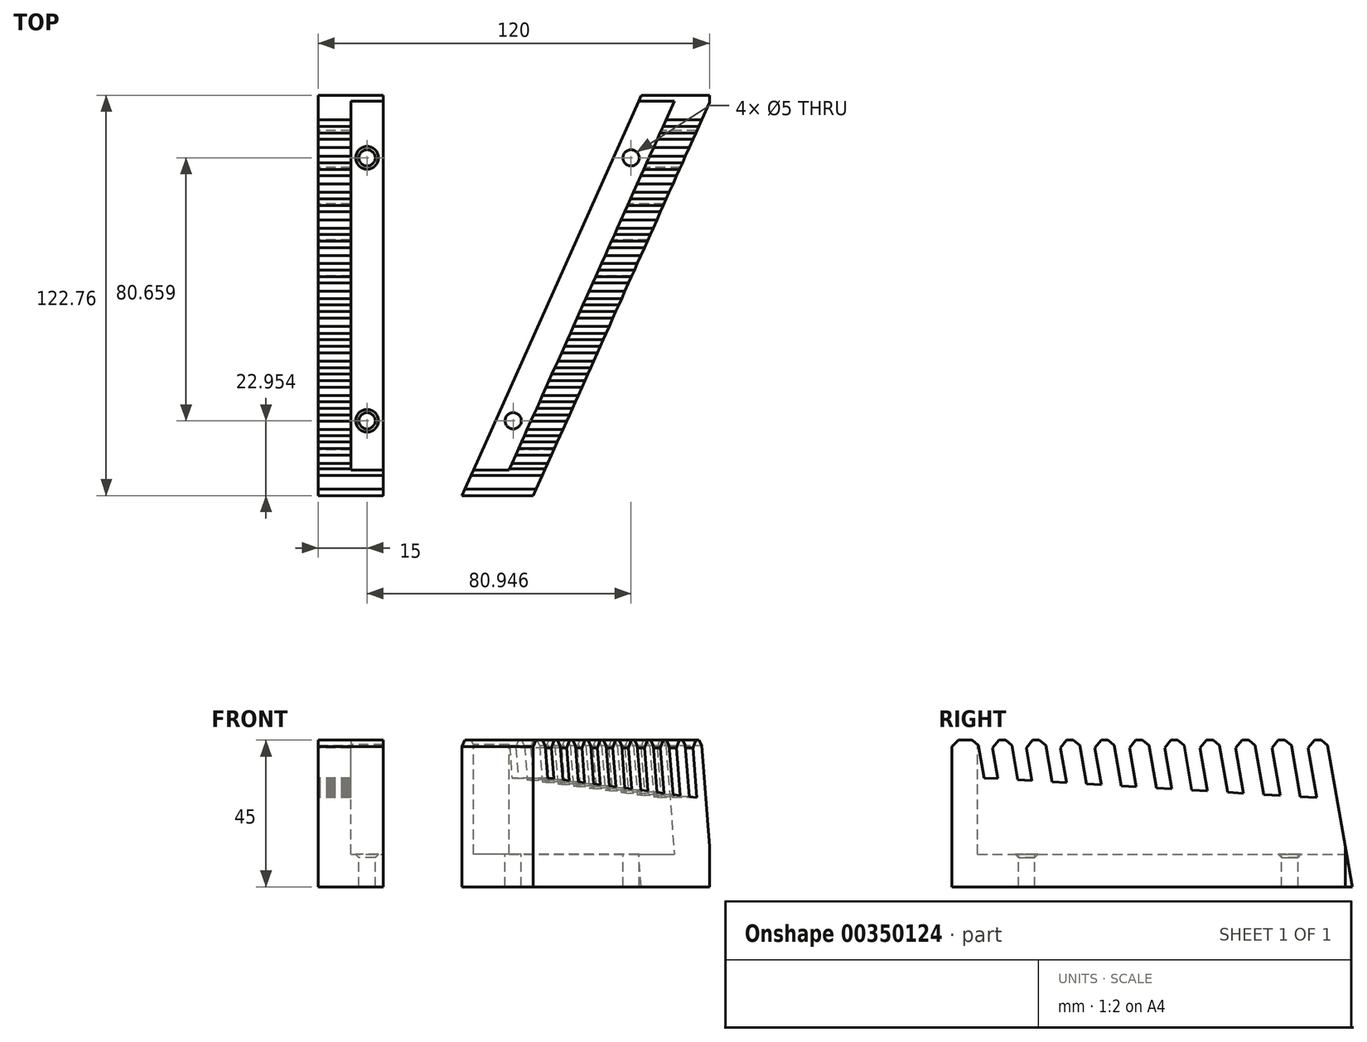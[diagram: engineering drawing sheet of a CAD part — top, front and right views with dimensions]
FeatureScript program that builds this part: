
annotation { "Feature Type Name" : "Feature", "Feature Type Description" : "" }
export const myFeature = defineFeature(function(context is Context, id is Id, definition is map)
    precondition{}
    {
        {
            var Q0;
            Q0=qCreatedBy(makeId("Right.planeOp"),FACE);
            var sketch = newSketch(context, id + "F0", { "sketchPlane" : qUnion([Q0])});
            skLineSegment(sketch, "E0.bottom", {"start": v(0, 0) * mm, "end": v(122.76, 0) * mm});
            skLineSegment(sketch, "E0.top", {"start": v(0, 45) * mm, "end": v(7.9, 45) * mm});
            skLineSegment(sketch, "E0.left", {"start": v(0, 0) * mm, "end": v(0, 45) * mm});
            skLineSegment(sketch, "E1", {"start": v(7.9, 45) * mm, "end": v(9.9, 33.41) * mm});
            skLineSegment(sketch, "E2", {"start": v(12.05, 45) * mm, "end": v(14.1, 33.16) * mm});
            skLineSegment(sketch, "E3", {"start": v(18.14, 45) * mm, "end": v(20.26, 32.8) * mm});
            skLineSegment(sketch, "E4", {"start": v(22.4, 45) * mm, "end": v(24.56, 32.54) * mm});
            skLineSegment(sketch, "E5", {"start": v(28.5, 45) * mm, "end": v(30.72, 32.18) * mm});
            skLineSegment(sketch, "E6", {"start": v(32.86, 45) * mm, "end": v(35.13, 31.92) * mm});
            skLineSegment(sketch, "E7", {"start": v(38.95, 45) * mm, "end": v(41.28, 31.55) * mm});
            skLineSegment(sketch, "E8", {"start": v(43.41, 45) * mm, "end": v(45.8, 31.29) * mm});
            skLineSegment(sketch, "E9", {"start": v(49.5, 45) * mm, "end": v(51.94, 30.92) * mm});
            skLineSegment(sketch, "E10", {"start": v(54.07, 45) * mm, "end": v(56.56, 30.65) * mm});
            skLineSegment(sketch, "E11", {"start": v(60.16, 45) * mm, "end": v(62.71, 30.28) * mm});
            skLineSegment(sketch, "E12", {"start": v(64.83, 45) * mm, "end": v(67.43, 30) * mm});
            skLineSegment(sketch, "E13", {"start": v(70.92, 45) * mm, "end": v(73.58, 29.64) * mm});
            skLineSegment(sketch, "E14", {"start": v(75.69, 45) * mm, "end": v(78.4, 29.35) * mm});
            skLineSegment(sketch, "E15", {"start": v(81.78, 45) * mm, "end": v(84.55, 28.99) * mm});
            skLineSegment(sketch, "E16", {"start": v(86.65, 45) * mm, "end": v(89.47, 28.7) * mm});
            skLineSegment(sketch, "E17", {"start": v(92.74, 45) * mm, "end": v(95.63, 28.33) * mm});
            skLineSegment(sketch, "E18", {"start": v(97.71, 45) * mm, "end": v(100.65, 28.03) * mm});
            skLineSegment(sketch, "E19", {"start": v(103.8, 45) * mm, "end": v(106.8, 27.67) * mm});
            skLineSegment(sketch, "E20", {"start": v(108.88, 45) * mm, "end": v(111.93, 27.36) * mm});
            skLineSegment(sketch, "E21", {"start": v(114.97, 45) * mm, "end": v(117.16, 32.36) * mm});
            skLineSegment(sketch, "E22.trimOffspring", {"start": v(12.05, 45) * mm, "end": v(18.14, 45) * mm});
            skLineSegment(sketch, "E23.trimOffspring", {"start": v(22.4, 45) * mm, "end": v(28.5, 45) * mm});
            skLineSegment(sketch, "E24.trimOffspring", {"start": v(32.86, 45) * mm, "end": v(38.95, 45) * mm});
            skLineSegment(sketch, "E25.trimOffspring", {"start": v(43.41, 45) * mm, "end": v(49.5, 45) * mm});
            skLineSegment(sketch, "E26.trimOffspring", {"start": v(54.07, 45) * mm, "end": v(60.16, 45) * mm});
            skLineSegment(sketch, "E27.trimOffspring", {"start": v(64.83, 45) * mm, "end": v(70.92, 45) * mm});
            skLineSegment(sketch, "E28.trimOffspring", {"start": v(75.69, 45) * mm, "end": v(81.78, 45) * mm});
            skLineSegment(sketch, "E29.trimOffspring", {"start": v(86.65, 45) * mm, "end": v(92.74, 45) * mm});
            skLineSegment(sketch, "E30.trimOffspring", {"start": v(97.71, 45) * mm, "end": v(103.8, 45) * mm});
            skLineSegment(sketch, "E31.trimOffspring", {"start": v(108.88, 45) * mm, "end": v(114.97, 45) * mm});
            skLineSegment(sketch, "E32.trimOffspring", {"start": v(163.56, 45) * mm, "end": v(163.58, 45) * mm});
            skLineSegment(sketch, "E33", {"start": v(114.97, 45) * mm, "end": v(122.76, 0) * mm});
            skLineSegment(sketch, "E34", {"start": v(9.9, 33.41) * mm, "end": v(14.1, 33.16) * mm});
            skPoint(sketch, "E35.orphan", {"position": v(0, 34) * mm});
            skLineSegment(sketch, "E36.trimOffspring", {"start": v(20.26, 32.8) * mm, "end": v(24.56, 32.54) * mm});
            skLineSegment(sketch, "E37.trimOffspring", {"start": v(30.72, 32.18) * mm, "end": v(35.13, 31.92) * mm});
            skLineSegment(sketch, "E38.trimOffspring", {"start": v(41.28, 31.55) * mm, "end": v(45.8, 31.29) * mm});
            skLineSegment(sketch, "E39.trimOffspring", {"start": v(51.94, 30.92) * mm, "end": v(56.56, 30.65) * mm});
            skLineSegment(sketch, "E40.trimOffspring", {"start": v(62.71, 30.28) * mm, "end": v(67.43, 30) * mm});
            skLineSegment(sketch, "E41.trimOffspring", {"start": v(73.58, 29.64) * mm, "end": v(78.4, 29.35) * mm});
            skLineSegment(sketch, "E42.trimOffspring", {"start": v(84.55, 28.99) * mm, "end": v(89.47, 28.7) * mm});
            skLineSegment(sketch, "E43.trimOffspring", {"start": v(106.8, 27.67) * mm, "end": v(111.93, 27.36) * mm});
            skPoint(sketch, "E44.orphan", {"position": v(118.08, 27) * mm});
            skLineSegment(sketch, "E45", {"start": v(95.63, 28.33) * mm, "end": v(100.65, 28.03) * mm});
            skSolve(sketch);
        }
        {
            var Q0;
            Q0 = qSketchRegion(id + "F0", true);
            extrude(context, id + "F1", {"entities" : qUnion([Q0]), "depth" : 120 * mm});
        }
        {
            var Q0;
            Q0=makeQuery(id+"F1.opExtrude","SWEPT_FACE",FACE,{"disambiguationData":[OSD([sQuery(id+"F0.wireOp",EDGE,"E0.top")])]});
            var sketch = newSketch(context, id + "F2", { "sketchPlane" : qUnion([Q0])});
            skLineSegment(sketch, "E46", {"start": v(10, 122.56) * mm, "end": v(10, 0) * mm});
            skLineSegment(sketch, "E47", {"start": v(55, 0) * mm, "end": v(110, 122.75) * mm});
            skLineSegment(sketch, "E48", {"start": v(120.96, 122.75) * mm, "end": v(65.96, 0) * mm});
            skLineSegment(sketch, "E49", {"start": v(65.96, 0) * mm, "end": v(120, 0) * mm});
            skLineSegment(sketch, "E50", {"start": v(120.96, 122.75) * mm, "end": v(120.96, 0) * mm});
            skLineSegment(sketch, "E51", {"start": v(120.96, 0) * mm, "end": v(65.96, 0) * mm});
            skLineSegment(sketch, "E52", {"start": v(55, 0) * mm, "end": v(10, 0) * mm});
            skLineSegment(sketch, "E53", {"start": v(110, 122.75) * mm, "end": v(10, 122.56) * mm});
            skLineSegment(sketch, "E54", {"start": v(10, 0) * mm, "end": v(55, 0) * mm});
            skSolve(sketch);
        }
        {
            var Q0;
            {var subQ2=sQuery(id+"F0.wireOp",EDGE,"E0.top");var subQ6=makeQuery(id+"F1.opExtrude","CAP_EDGE",EDGE,{"disambiguationData":[OSD([subQ2])],"isStart":false});Q0=makeQuery(id+"F2.imprint","IMPRINT",FACE,{"disambiguationData":[TD([[makeQuery(id+"F2.imprint","IMPRINT",EDGE,{"derivedFrom":subQ6}),1.0]])]});}
            var Q1;
            {var subQ3=sQuery(id+"F2.wireOp",EDGE,"E50");Q1=makeQuery(id+"F2.imprint","IMPRINT",FACE,{"disambiguationData":[TD([[makeQuery(id+"F2.imprint","IMPRINT",EDGE,{"derivedFrom":subQ3}),-1.0]])]});}
            extrude(context, id + "F3", {"entities" : qUnion([Q0, Q1]), "operationType" : NewBodyOperationType.REMOVE, "endBound" : BoundingType.THROUGH_ALL, "oppositeDirection" : true, "depth" : 25 * mm});
        }
        {
            var Q0;
            {var subQ0=sQuery(id+"F2.wireOp",EDGE,"E53");Q0=makeQuery(id+"F2.imprint","IMPRINT",FACE,{"disambiguationData":[TD([[makeQuery(id+"F2.imprint","IMPRINT",EDGE,{"derivedFrom":subQ0}),1.0]])]});}
            var Q1;
            {var subQ0=sQuery(id+"F2.wireOp",EDGE,"E54");Q1=makeQuery(id+"F2.imprint","IMPRINT",FACE,{"disambiguationData":[TD([[makeQuery(id+"F2.imprint","IMPRINT",EDGE,{"derivedFrom":subQ0}),-1.0]])]});}
            extrude(context, id + "F4", {"entities" : qUnion([Q0, Q1]), "operationType" : NewBodyOperationType.REMOVE, "oppositeDirection" : true, "depth" : 35 * mm});
        }
        {
            var Q0;
            {var subQ0=sQuery(id+"F2.wireOp",EDGE,"E53");Q0=makeQuery(id+"F2.imprint","IMPRINT",FACE,{"disambiguationData":[TD([[makeQuery(id+"F2.imprint","IMPRINT",EDGE,{"derivedFrom":subQ0}),1.0]])]});}
            var sketch = newSketch(context, id + "F5", { "sketchPlane" : qUnion([Q0])});
            skLineSegment(sketch, "E55", {"start": v(20, 127.84) * mm, "end": v(20, -6.7) * mm});
            skLineSegment(sketch, "E56", {"start": v(101.32, 127.84) * mm, "end": v(41.04, -6.7) * mm});
            skLineSegment(sketch, "E57", {"start": v(20, 127.84) * mm, "end": v(101.32, 127.84) * mm});
            skLineSegment(sketch, "E58", {"start": v(20, -6.7) * mm, "end": v(41.04, -6.7) * mm});
            skSolve(sketch);
        }
        {
            var Q0;
            Q0 = qSketchRegion(id + "F5", true);
            extrude(context, id + "F6", {"entities" : qUnion([Q0]), "operationType" : NewBodyOperationType.REMOVE, "endBound" : BoundingType.THROUGH_ALL, "oppositeDirection" : true, "depth" : 25 * mm});
        }
        {
            var Q0;
            {var subQ0=sQuery(id+"F2.wireOp",EDGE,"E53");Q0=makeQuery(id+"F2.imprint","IMPRINT",FACE,{"disambiguationData":[TD([[makeQuery(id+"F2.imprint","IMPRINT",EDGE,{"derivedFrom":subQ0}),1.0]])]});}
            var sketch = newSketch(context, id + "F7", { "sketchPlane" : qUnion([Q0])});
            skCircle(sketch, "E59", {"center": v(15, 103.61) * mm, "radius": 2.5 * mm});
            skCircle(sketch, "E60", {"center": v(15, 22.95) * mm, "radius": 2.5 * mm});
            skCircle(sketch, "E61", {"center": v(95.95, 103.61) * mm, "radius": 2.5 * mm});
            skCircle(sketch, "E62", {"center": v(59.8, 22.95) * mm, "radius": 2.5 * mm});
            skSolve(sketch);
        }
        {
            var Q0;
            Q0=makeQuery(id+"F7.imprint","IMPRINT",FACE,{"disambiguationData":[TD([[makeQuery(id+"F7.imprint","IMPRINT",EDGE,{"derivedFrom":sQuery(id+"F7.wireOp",EDGE,"E59")}),1.0]])]});
            var Q1;
            Q1=makeQuery(id+"F7.imprint","IMPRINT",FACE,{"disambiguationData":[TD([[makeQuery(id+"F7.imprint","IMPRINT",EDGE,{"derivedFrom":sQuery(id+"F7.wireOp",EDGE,"E61")}),1.0]])]});
            var Q2;
            Q2=makeQuery(id+"F7.imprint","IMPRINT",FACE,{"disambiguationData":[TD([[makeQuery(id+"F7.imprint","IMPRINT",EDGE,{"derivedFrom":sQuery(id+"F7.wireOp",EDGE,"E60")}),1.0]])]});
            var Q3;
            Q3=makeQuery(id+"F7.imprint","IMPRINT",FACE,{"disambiguationData":[TD([[makeQuery(id+"F7.imprint","IMPRINT",EDGE,{"derivedFrom":sQuery(id+"F7.wireOp",EDGE,"E62")}),1.0]])]});
            extrude(context, id + "F8", {"entities" : qUnion([Q0, Q1, Q2, Q3]), "operationType" : NewBodyOperationType.REMOVE, "oppositeDirection" : true, "depth" : 55.9 * mm});
        }
        {
            var Q0;
            Q0=makeQuery(id+"F7.imprint","IMPRINT",FACE,{"disambiguationData":[TD([[makeQuery(id+"F7.imprint","IMPRINT",EDGE,{"derivedFrom":sQuery(id+"F7.wireOp",EDGE,"E61")}),1.0]])]});
            var Q1;
            Q1=makeQuery(id+"F7.imprint","IMPRINT",FACE,{"disambiguationData":[TD([[makeQuery(id+"F7.imprint","IMPRINT",EDGE,{"derivedFrom":sQuery(id+"F7.wireOp",EDGE,"E62")}),1.0]])]});
            extrude(context, id + "F9", {"entities" : qUnion([Q0, Q1]), "operationType" : NewBodyOperationType.REMOVE, "oppositeDirection" : true, "depth" : 56 * mm});
        }
        {
            var Q0;
            {var subQ0=sQuery(id+"F0.wireOp",EDGE,"E33");var subQ1=sQuery(id+"F0.wireOp",EDGE,"E31.trimOffspring");Q0=makeQuery(id+"F4.boolean.opBoolean","SPLIT",EDGE,{"disambiguationData":[TD([makeQuery(id+"F4.opExtrude","SWEPT_FACE",FACE,{"disambiguationData":[OSD([sQuery(id+"F2.wireOp",EDGE,"E46")])]})])],"derivedFrom":makeQuery(id+"F1.opExtrude","SWEPT_EDGE",EDGE,{"disambiguationData":[OSD([subQ1,subQ0])]})});}
            var Q1;
            {var subQ0=sQuery(id+"F0.wireOp",EDGE,"E31.trimOffspring");var subQ1=sQuery(id+"F0.wireOp",EDGE,"E20");Q1=makeQuery(id+"F4.boolean.opBoolean","SPLIT",EDGE,{"disambiguationData":[TD([makeQuery(id+"F4.opExtrude","SWEPT_FACE",FACE,{"disambiguationData":[OSD([sQuery(id+"F2.wireOp",EDGE,"E46")])]})])],"derivedFrom":makeQuery(id+"F1.opExtrude","SWEPT_EDGE",EDGE,{"disambiguationData":[OSD([subQ1,subQ0])]})});}
            var Q2;
            {var subQ0=sQuery(id+"F0.wireOp",EDGE,"E30.trimOffspring");var subQ1=sQuery(id+"F0.wireOp",EDGE,"E19");Q2=makeQuery(id+"F4.boolean.opBoolean","SPLIT",EDGE,{"disambiguationData":[TD([makeQuery(id+"F4.opExtrude","SWEPT_FACE",FACE,{"disambiguationData":[OSD([sQuery(id+"F2.wireOp",EDGE,"E46")])]})])],"derivedFrom":makeQuery(id+"F1.opExtrude","SWEPT_EDGE",EDGE,{"disambiguationData":[OSD([subQ1,subQ0])]})});}
            var Q3;
            {var subQ0=sQuery(id+"F0.wireOp",EDGE,"E30.trimOffspring");var subQ1=sQuery(id+"F0.wireOp",EDGE,"E18");Q3=makeQuery(id+"F4.boolean.opBoolean","SPLIT",EDGE,{"disambiguationData":[TD([makeQuery(id+"F4.opExtrude","SWEPT_FACE",FACE,{"disambiguationData":[OSD([sQuery(id+"F2.wireOp",EDGE,"E46")])]})])],"derivedFrom":makeQuery(id+"F1.opExtrude","SWEPT_EDGE",EDGE,{"disambiguationData":[OSD([subQ1,subQ0])]})});}
            var Q4;
            {var subQ0=sQuery(id+"F0.wireOp",EDGE,"E29.trimOffspring");var subQ1=sQuery(id+"F0.wireOp",EDGE,"E17");Q4=makeQuery(id+"F4.boolean.opBoolean","SPLIT",EDGE,{"disambiguationData":[TD([makeQuery(id+"F4.opExtrude","SWEPT_FACE",FACE,{"disambiguationData":[OSD([sQuery(id+"F2.wireOp",EDGE,"E46")])]})])],"derivedFrom":makeQuery(id+"F1.opExtrude","SWEPT_EDGE",EDGE,{"disambiguationData":[OSD([subQ1,subQ0])]})});}
            var Q5;
            {var subQ0=sQuery(id+"F0.wireOp",EDGE,"E29.trimOffspring");var subQ1=sQuery(id+"F0.wireOp",EDGE,"E16");Q5=makeQuery(id+"F4.boolean.opBoolean","SPLIT",EDGE,{"disambiguationData":[TD([makeQuery(id+"F4.opExtrude","SWEPT_FACE",FACE,{"disambiguationData":[OSD([sQuery(id+"F2.wireOp",EDGE,"E46")])]})])],"derivedFrom":makeQuery(id+"F1.opExtrude","SWEPT_EDGE",EDGE,{"disambiguationData":[OSD([subQ1,subQ0])]})});}
            var Q6;
            {var subQ0=sQuery(id+"F0.wireOp",EDGE,"E28.trimOffspring");var subQ1=sQuery(id+"F0.wireOp",EDGE,"E15");Q6=makeQuery(id+"F4.boolean.opBoolean","SPLIT",EDGE,{"disambiguationData":[TD([makeQuery(id+"F4.opExtrude","SWEPT_FACE",FACE,{"disambiguationData":[OSD([sQuery(id+"F2.wireOp",EDGE,"E46")])]})])],"derivedFrom":makeQuery(id+"F1.opExtrude","SWEPT_EDGE",EDGE,{"disambiguationData":[OSD([subQ1,subQ0])]})});}
            var Q7;
            {var subQ0=sQuery(id+"F0.wireOp",EDGE,"E28.trimOffspring");var subQ1=sQuery(id+"F0.wireOp",EDGE,"E14");Q7=makeQuery(id+"F4.boolean.opBoolean","SPLIT",EDGE,{"disambiguationData":[TD([makeQuery(id+"F4.opExtrude","SWEPT_FACE",FACE,{"disambiguationData":[OSD([sQuery(id+"F2.wireOp",EDGE,"E46")])]})])],"derivedFrom":makeQuery(id+"F1.opExtrude","SWEPT_EDGE",EDGE,{"disambiguationData":[OSD([subQ1,subQ0])]})});}
            var Q8;
            {var subQ0=sQuery(id+"F0.wireOp",EDGE,"E27.trimOffspring");var subQ1=sQuery(id+"F0.wireOp",EDGE,"E13");Q8=makeQuery(id+"F4.boolean.opBoolean","SPLIT",EDGE,{"disambiguationData":[TD([makeQuery(id+"F4.opExtrude","SWEPT_FACE",FACE,{"disambiguationData":[OSD([sQuery(id+"F2.wireOp",EDGE,"E46")])]})])],"derivedFrom":makeQuery(id+"F1.opExtrude","SWEPT_EDGE",EDGE,{"disambiguationData":[OSD([subQ1,subQ0])]})});}
            var Q9;
            {var subQ0=sQuery(id+"F0.wireOp",EDGE,"E27.trimOffspring");var subQ1=sQuery(id+"F0.wireOp",EDGE,"E12");Q9=makeQuery(id+"F4.boolean.opBoolean","SPLIT",EDGE,{"disambiguationData":[TD([makeQuery(id+"F4.opExtrude","SWEPT_FACE",FACE,{"disambiguationData":[OSD([sQuery(id+"F2.wireOp",EDGE,"E46")])]})])],"derivedFrom":makeQuery(id+"F1.opExtrude","SWEPT_EDGE",EDGE,{"disambiguationData":[OSD([subQ1,subQ0])]})});}
            var Q10;
            {var subQ0=sQuery(id+"F0.wireOp",EDGE,"E26.trimOffspring");var subQ1=sQuery(id+"F0.wireOp",EDGE,"E11");Q10=makeQuery(id+"F4.boolean.opBoolean","SPLIT",EDGE,{"disambiguationData":[TD([makeQuery(id+"F4.opExtrude","SWEPT_FACE",FACE,{"disambiguationData":[OSD([sQuery(id+"F2.wireOp",EDGE,"E46")])]})])],"derivedFrom":makeQuery(id+"F1.opExtrude","SWEPT_EDGE",EDGE,{"disambiguationData":[OSD([subQ1,subQ0])]})});}
            var Q11;
            {var subQ0=sQuery(id+"F0.wireOp",EDGE,"E26.trimOffspring");var subQ1=sQuery(id+"F0.wireOp",EDGE,"E10");Q11=makeQuery(id+"F4.boolean.opBoolean","SPLIT",EDGE,{"disambiguationData":[TD([makeQuery(id+"F4.opExtrude","SWEPT_FACE",FACE,{"disambiguationData":[OSD([sQuery(id+"F2.wireOp",EDGE,"E46")])]})])],"derivedFrom":makeQuery(id+"F1.opExtrude","SWEPT_EDGE",EDGE,{"disambiguationData":[OSD([subQ1,subQ0])]})});}
            var Q12;
            {var subQ0=sQuery(id+"F0.wireOp",EDGE,"E25.trimOffspring");var subQ1=sQuery(id+"F0.wireOp",EDGE,"E9");Q12=makeQuery(id+"F4.boolean.opBoolean","SPLIT",EDGE,{"disambiguationData":[TD([makeQuery(id+"F4.opExtrude","SWEPT_FACE",FACE,{"disambiguationData":[OSD([sQuery(id+"F2.wireOp",EDGE,"E46")])]})])],"derivedFrom":makeQuery(id+"F1.opExtrude","SWEPT_EDGE",EDGE,{"disambiguationData":[OSD([subQ1,subQ0])]})});}
            var Q13;
            {var subQ0=sQuery(id+"F0.wireOp",EDGE,"E25.trimOffspring");var subQ1=sQuery(id+"F0.wireOp",EDGE,"E8");Q13=makeQuery(id+"F4.boolean.opBoolean","SPLIT",EDGE,{"disambiguationData":[TD([makeQuery(id+"F4.opExtrude","SWEPT_FACE",FACE,{"disambiguationData":[OSD([sQuery(id+"F2.wireOp",EDGE,"E46")])]})])],"derivedFrom":makeQuery(id+"F1.opExtrude","SWEPT_EDGE",EDGE,{"disambiguationData":[OSD([subQ1,subQ0])]})});}
            var Q14;
            {var subQ0=sQuery(id+"F0.wireOp",EDGE,"E24.trimOffspring");var subQ1=sQuery(id+"F0.wireOp",EDGE,"E7");Q14=makeQuery(id+"F4.boolean.opBoolean","SPLIT",EDGE,{"disambiguationData":[TD([makeQuery(id+"F4.opExtrude","SWEPT_FACE",FACE,{"disambiguationData":[OSD([sQuery(id+"F2.wireOp",EDGE,"E46")])]})])],"derivedFrom":makeQuery(id+"F1.opExtrude","SWEPT_EDGE",EDGE,{"disambiguationData":[OSD([subQ1,subQ0])]})});}
            var Q15;
            {var subQ0=sQuery(id+"F0.wireOp",EDGE,"E24.trimOffspring");var subQ1=sQuery(id+"F0.wireOp",EDGE,"E6");Q15=makeQuery(id+"F4.boolean.opBoolean","SPLIT",EDGE,{"disambiguationData":[TD([makeQuery(id+"F4.opExtrude","SWEPT_FACE",FACE,{"disambiguationData":[OSD([sQuery(id+"F2.wireOp",EDGE,"E46")])]})])],"derivedFrom":makeQuery(id+"F1.opExtrude","SWEPT_EDGE",EDGE,{"disambiguationData":[OSD([subQ1,subQ0])]})});}
            var Q16;
            {var subQ0=sQuery(id+"F0.wireOp",EDGE,"E23.trimOffspring");var subQ1=sQuery(id+"F0.wireOp",EDGE,"E5");Q16=makeQuery(id+"F4.boolean.opBoolean","SPLIT",EDGE,{"disambiguationData":[TD([makeQuery(id+"F4.opExtrude","SWEPT_FACE",FACE,{"disambiguationData":[OSD([sQuery(id+"F2.wireOp",EDGE,"E46")])]})])],"derivedFrom":makeQuery(id+"F1.opExtrude","SWEPT_EDGE",EDGE,{"disambiguationData":[OSD([subQ1,subQ0])]})});}
            var Q17;
            {var subQ0=sQuery(id+"F0.wireOp",EDGE,"E23.trimOffspring");var subQ1=sQuery(id+"F0.wireOp",EDGE,"E4");Q17=makeQuery(id+"F4.boolean.opBoolean","SPLIT",EDGE,{"disambiguationData":[TD([makeQuery(id+"F4.opExtrude","SWEPT_FACE",FACE,{"disambiguationData":[OSD([sQuery(id+"F2.wireOp",EDGE,"E46")])]})])],"derivedFrom":makeQuery(id+"F1.opExtrude","SWEPT_EDGE",EDGE,{"disambiguationData":[OSD([subQ1,subQ0])]})});}
            var Q18;
            {var subQ0=sQuery(id+"F0.wireOp",EDGE,"E22.trimOffspring");var subQ1=sQuery(id+"F0.wireOp",EDGE,"E3");Q18=makeQuery(id+"F4.boolean.opBoolean","SPLIT",EDGE,{"disambiguationData":[TD([makeQuery(id+"F4.opExtrude","SWEPT_FACE",FACE,{"disambiguationData":[OSD([sQuery(id+"F2.wireOp",EDGE,"E46")])]})])],"derivedFrom":makeQuery(id+"F1.opExtrude","SWEPT_EDGE",EDGE,{"disambiguationData":[OSD([subQ1,subQ0])]})});}
            var Q19;
            {var subQ0=sQuery(id+"F0.wireOp",EDGE,"E22.trimOffspring");var subQ1=sQuery(id+"F0.wireOp",EDGE,"E2");Q19=makeQuery(id+"F4.boolean.opBoolean","SPLIT",EDGE,{"disambiguationData":[TD([makeQuery(id+"F4.opExtrude","SWEPT_FACE",FACE,{"disambiguationData":[OSD([sQuery(id+"F2.wireOp",EDGE,"E46")])]})])],"derivedFrom":makeQuery(id+"F1.opExtrude","SWEPT_EDGE",EDGE,{"disambiguationData":[OSD([subQ1,subQ0])]})});}
            var Q20;
            {var subQ0=sQuery(id+"F0.wireOp",EDGE,"E1");var subQ1=sQuery(id+"F0.wireOp",EDGE,"E0.top");Q20=makeQuery(id+"F4.boolean.opBoolean","SPLIT",EDGE,{"disambiguationData":[TD([makeQuery(id+"F4.opExtrude","SWEPT_FACE",FACE,{"disambiguationData":[OSD([sQuery(id+"F2.wireOp",EDGE,"E46")])]})])],"derivedFrom":makeQuery(id+"F1.opExtrude","SWEPT_EDGE",EDGE,{"disambiguationData":[OSD([subQ1,subQ0])]})});}
            var Q21;
            {var subQ0=sQuery(id+"F0.wireOp",EDGE,"E0.left");var subQ1=sQuery(id+"F0.wireOp",EDGE,"E0.top");Q21=makeQuery(id+"F4.boolean.opBoolean","SPLIT",EDGE,{"disambiguationData":[TD([makeQuery(id+"F4.opExtrude","SWEPT_FACE",FACE,{"disambiguationData":[OSD([sQuery(id+"F2.wireOp",EDGE,"E46")])]})])],"derivedFrom":makeQuery(id+"F1.opExtrude","SWEPT_EDGE",EDGE,{"disambiguationData":[OSD([subQ1,subQ0])]})});}
            var Q22;
            {var subQ0=sQuery(id+"F0.wireOp",EDGE,"E0.top");var subQ1=sQuery(id+"F0.wireOp",EDGE,"E0.left");Q22=makeQuery(id+"F4.boolean.opBoolean","SPLIT",EDGE,{"disambiguationData":[TD([makeQuery(id+"F3.boolean.opBoolean","COPY",FACE,{"derivedFrom":makeQuery(id+"F3.opExtrude","SWEPT_FACE",FACE,{"disambiguationData":[OSD([sQuery(id+"F2.wireOp",EDGE,"E48")])]})})])],"derivedFrom":makeQuery(id+"F1.opExtrude","SWEPT_EDGE",EDGE,{"disambiguationData":[OSD([subQ0,subQ1])]})});}
            var Q23;
            {var subQ0=sQuery(id+"F0.wireOp",EDGE,"E0.top");var subQ1=sQuery(id+"F0.wireOp",EDGE,"E1");Q23=makeQuery(id+"F4.boolean.opBoolean","SPLIT",EDGE,{"disambiguationData":[TD([makeQuery(id+"F3.boolean.opBoolean","COPY",FACE,{"derivedFrom":makeQuery(id+"F3.opExtrude","SWEPT_FACE",FACE,{"disambiguationData":[OSD([sQuery(id+"F2.wireOp",EDGE,"E48")])]})})])],"derivedFrom":makeQuery(id+"F1.opExtrude","SWEPT_EDGE",EDGE,{"disambiguationData":[OSD([subQ0,subQ1])]})});}
            var Q24;
            {var subQ0=sQuery(id+"F0.wireOp",EDGE,"E2");var subQ1=sQuery(id+"F0.wireOp",EDGE,"E22.trimOffspring");Q24=makeQuery(id+"F4.boolean.opBoolean","SPLIT",EDGE,{"disambiguationData":[TD([makeQuery(id+"F3.boolean.opBoolean","COPY",FACE,{"derivedFrom":makeQuery(id+"F3.opExtrude","SWEPT_FACE",FACE,{"disambiguationData":[OSD([sQuery(id+"F2.wireOp",EDGE,"E48")])]})})])],"derivedFrom":makeQuery(id+"F1.opExtrude","SWEPT_EDGE",EDGE,{"disambiguationData":[OSD([subQ0,subQ1])]})});}
            var Q25;
            {var subQ0=sQuery(id+"F0.wireOp",EDGE,"E3");var subQ1=sQuery(id+"F0.wireOp",EDGE,"E22.trimOffspring");Q25=makeQuery(id+"F4.boolean.opBoolean","SPLIT",EDGE,{"disambiguationData":[TD([makeQuery(id+"F3.boolean.opBoolean","COPY",FACE,{"derivedFrom":makeQuery(id+"F3.opExtrude","SWEPT_FACE",FACE,{"disambiguationData":[OSD([sQuery(id+"F2.wireOp",EDGE,"E48")])]})})])],"derivedFrom":makeQuery(id+"F1.opExtrude","SWEPT_EDGE",EDGE,{"disambiguationData":[OSD([subQ0,subQ1])]})});}
            var Q26;
            {var subQ0=sQuery(id+"F0.wireOp",EDGE,"E4");var subQ1=sQuery(id+"F0.wireOp",EDGE,"E23.trimOffspring");Q26=makeQuery(id+"F4.boolean.opBoolean","SPLIT",EDGE,{"disambiguationData":[TD([makeQuery(id+"F3.boolean.opBoolean","COPY",FACE,{"derivedFrom":makeQuery(id+"F3.opExtrude","SWEPT_FACE",FACE,{"disambiguationData":[OSD([sQuery(id+"F2.wireOp",EDGE,"E48")])]})})])],"derivedFrom":makeQuery(id+"F1.opExtrude","SWEPT_EDGE",EDGE,{"disambiguationData":[OSD([subQ0,subQ1])]})});}
            var Q27;
            {var subQ0=sQuery(id+"F0.wireOp",EDGE,"E5");var subQ1=sQuery(id+"F0.wireOp",EDGE,"E23.trimOffspring");Q27=makeQuery(id+"F4.boolean.opBoolean","SPLIT",EDGE,{"disambiguationData":[TD([makeQuery(id+"F3.boolean.opBoolean","COPY",FACE,{"derivedFrom":makeQuery(id+"F3.opExtrude","SWEPT_FACE",FACE,{"disambiguationData":[OSD([sQuery(id+"F2.wireOp",EDGE,"E48")])]})})])],"derivedFrom":makeQuery(id+"F1.opExtrude","SWEPT_EDGE",EDGE,{"disambiguationData":[OSD([subQ0,subQ1])]})});}
            var Q28;
            {var subQ0=sQuery(id+"F0.wireOp",EDGE,"E6");var subQ1=sQuery(id+"F0.wireOp",EDGE,"E24.trimOffspring");Q28=makeQuery(id+"F4.boolean.opBoolean","SPLIT",EDGE,{"disambiguationData":[TD([makeQuery(id+"F3.boolean.opBoolean","COPY",FACE,{"derivedFrom":makeQuery(id+"F3.opExtrude","SWEPT_FACE",FACE,{"disambiguationData":[OSD([sQuery(id+"F2.wireOp",EDGE,"E48")])]})})])],"derivedFrom":makeQuery(id+"F1.opExtrude","SWEPT_EDGE",EDGE,{"disambiguationData":[OSD([subQ0,subQ1])]})});}
            var Q29;
            {var subQ0=sQuery(id+"F0.wireOp",EDGE,"E7");var subQ1=sQuery(id+"F0.wireOp",EDGE,"E24.trimOffspring");Q29=makeQuery(id+"F4.boolean.opBoolean","SPLIT",EDGE,{"disambiguationData":[TD([makeQuery(id+"F3.boolean.opBoolean","COPY",FACE,{"derivedFrom":makeQuery(id+"F3.opExtrude","SWEPT_FACE",FACE,{"disambiguationData":[OSD([sQuery(id+"F2.wireOp",EDGE,"E48")])]})})])],"derivedFrom":makeQuery(id+"F1.opExtrude","SWEPT_EDGE",EDGE,{"disambiguationData":[OSD([subQ0,subQ1])]})});}
            var Q30;
            {var subQ0=sQuery(id+"F0.wireOp",EDGE,"E8");var subQ1=sQuery(id+"F0.wireOp",EDGE,"E25.trimOffspring");Q30=makeQuery(id+"F4.boolean.opBoolean","SPLIT",EDGE,{"disambiguationData":[TD([makeQuery(id+"F3.boolean.opBoolean","COPY",FACE,{"derivedFrom":makeQuery(id+"F3.opExtrude","SWEPT_FACE",FACE,{"disambiguationData":[OSD([sQuery(id+"F2.wireOp",EDGE,"E48")])]})})])],"derivedFrom":makeQuery(id+"F1.opExtrude","SWEPT_EDGE",EDGE,{"disambiguationData":[OSD([subQ0,subQ1])]})});}
            var Q31;
            {var subQ0=sQuery(id+"F0.wireOp",EDGE,"E9");var subQ1=sQuery(id+"F0.wireOp",EDGE,"E25.trimOffspring");Q31=makeQuery(id+"F4.boolean.opBoolean","SPLIT",EDGE,{"disambiguationData":[TD([makeQuery(id+"F3.boolean.opBoolean","COPY",FACE,{"derivedFrom":makeQuery(id+"F3.opExtrude","SWEPT_FACE",FACE,{"disambiguationData":[OSD([sQuery(id+"F2.wireOp",EDGE,"E48")])]})})])],"derivedFrom":makeQuery(id+"F1.opExtrude","SWEPT_EDGE",EDGE,{"disambiguationData":[OSD([subQ0,subQ1])]})});}
            var Q32;
            {var subQ0=sQuery(id+"F0.wireOp",EDGE,"E10");var subQ1=sQuery(id+"F0.wireOp",EDGE,"E26.trimOffspring");Q32=makeQuery(id+"F4.boolean.opBoolean","SPLIT",EDGE,{"disambiguationData":[TD([makeQuery(id+"F3.boolean.opBoolean","COPY",FACE,{"derivedFrom":makeQuery(id+"F3.opExtrude","SWEPT_FACE",FACE,{"disambiguationData":[OSD([sQuery(id+"F2.wireOp",EDGE,"E48")])]})})])],"derivedFrom":makeQuery(id+"F1.opExtrude","SWEPT_EDGE",EDGE,{"disambiguationData":[OSD([subQ0,subQ1])]})});}
            var Q33;
            {var subQ0=sQuery(id+"F0.wireOp",EDGE,"E11");var subQ1=sQuery(id+"F0.wireOp",EDGE,"E26.trimOffspring");Q33=makeQuery(id+"F4.boolean.opBoolean","SPLIT",EDGE,{"disambiguationData":[TD([makeQuery(id+"F3.boolean.opBoolean","COPY",FACE,{"derivedFrom":makeQuery(id+"F3.opExtrude","SWEPT_FACE",FACE,{"disambiguationData":[OSD([sQuery(id+"F2.wireOp",EDGE,"E48")])]})})])],"derivedFrom":makeQuery(id+"F1.opExtrude","SWEPT_EDGE",EDGE,{"disambiguationData":[OSD([subQ0,subQ1])]})});}
            var Q34;
            {var subQ0=sQuery(id+"F0.wireOp",EDGE,"E12");var subQ1=sQuery(id+"F0.wireOp",EDGE,"E27.trimOffspring");Q34=makeQuery(id+"F4.boolean.opBoolean","SPLIT",EDGE,{"disambiguationData":[TD([makeQuery(id+"F3.boolean.opBoolean","COPY",FACE,{"derivedFrom":makeQuery(id+"F3.opExtrude","SWEPT_FACE",FACE,{"disambiguationData":[OSD([sQuery(id+"F2.wireOp",EDGE,"E48")])]})})])],"derivedFrom":makeQuery(id+"F1.opExtrude","SWEPT_EDGE",EDGE,{"disambiguationData":[OSD([subQ0,subQ1])]})});}
            var Q35;
            {var subQ0=sQuery(id+"F0.wireOp",EDGE,"E13");var subQ1=sQuery(id+"F0.wireOp",EDGE,"E27.trimOffspring");Q35=makeQuery(id+"F4.boolean.opBoolean","SPLIT",EDGE,{"disambiguationData":[TD([makeQuery(id+"F3.boolean.opBoolean","COPY",FACE,{"derivedFrom":makeQuery(id+"F3.opExtrude","SWEPT_FACE",FACE,{"disambiguationData":[OSD([sQuery(id+"F2.wireOp",EDGE,"E48")])]})})])],"derivedFrom":makeQuery(id+"F1.opExtrude","SWEPT_EDGE",EDGE,{"disambiguationData":[OSD([subQ0,subQ1])]})});}
            var Q36;
            {var subQ0=sQuery(id+"F0.wireOp",EDGE,"E14");var subQ1=sQuery(id+"F0.wireOp",EDGE,"E28.trimOffspring");Q36=makeQuery(id+"F4.boolean.opBoolean","SPLIT",EDGE,{"disambiguationData":[TD([makeQuery(id+"F3.boolean.opBoolean","COPY",FACE,{"derivedFrom":makeQuery(id+"F3.opExtrude","SWEPT_FACE",FACE,{"disambiguationData":[OSD([sQuery(id+"F2.wireOp",EDGE,"E48")])]})})])],"derivedFrom":makeQuery(id+"F1.opExtrude","SWEPT_EDGE",EDGE,{"disambiguationData":[OSD([subQ0,subQ1])]})});}
            var Q37;
            {var subQ0=sQuery(id+"F0.wireOp",EDGE,"E15");var subQ1=sQuery(id+"F0.wireOp",EDGE,"E28.trimOffspring");Q37=makeQuery(id+"F4.boolean.opBoolean","SPLIT",EDGE,{"disambiguationData":[TD([makeQuery(id+"F3.boolean.opBoolean","COPY",FACE,{"derivedFrom":makeQuery(id+"F3.opExtrude","SWEPT_FACE",FACE,{"disambiguationData":[OSD([sQuery(id+"F2.wireOp",EDGE,"E48")])]})})])],"derivedFrom":makeQuery(id+"F1.opExtrude","SWEPT_EDGE",EDGE,{"disambiguationData":[OSD([subQ0,subQ1])]})});}
            var Q38;
            {var subQ0=sQuery(id+"F0.wireOp",EDGE,"E16");var subQ1=sQuery(id+"F0.wireOp",EDGE,"E29.trimOffspring");Q38=makeQuery(id+"F4.boolean.opBoolean","SPLIT",EDGE,{"disambiguationData":[TD([makeQuery(id+"F3.boolean.opBoolean","COPY",FACE,{"derivedFrom":makeQuery(id+"F3.opExtrude","SWEPT_FACE",FACE,{"disambiguationData":[OSD([sQuery(id+"F2.wireOp",EDGE,"E48")])]})})])],"derivedFrom":makeQuery(id+"F1.opExtrude","SWEPT_EDGE",EDGE,{"disambiguationData":[OSD([subQ0,subQ1])]})});}
            var Q39;
            {var subQ0=sQuery(id+"F0.wireOp",EDGE,"E17");var subQ1=sQuery(id+"F0.wireOp",EDGE,"E29.trimOffspring");Q39=makeQuery(id+"F4.boolean.opBoolean","SPLIT",EDGE,{"disambiguationData":[TD([makeQuery(id+"F3.boolean.opBoolean","COPY",FACE,{"derivedFrom":makeQuery(id+"F3.opExtrude","SWEPT_FACE",FACE,{"disambiguationData":[OSD([sQuery(id+"F2.wireOp",EDGE,"E48")])]})})])],"derivedFrom":makeQuery(id+"F1.opExtrude","SWEPT_EDGE",EDGE,{"disambiguationData":[OSD([subQ0,subQ1])]})});}
            var Q40;
            {var subQ0=sQuery(id+"F0.wireOp",EDGE,"E18");var subQ1=sQuery(id+"F0.wireOp",EDGE,"E30.trimOffspring");Q40=makeQuery(id+"F4.boolean.opBoolean","SPLIT",EDGE,{"disambiguationData":[TD([makeQuery(id+"F3.boolean.opBoolean","COPY",FACE,{"derivedFrom":makeQuery(id+"F3.opExtrude","SWEPT_FACE",FACE,{"disambiguationData":[OSD([sQuery(id+"F2.wireOp",EDGE,"E48")])]})})])],"derivedFrom":makeQuery(id+"F1.opExtrude","SWEPT_EDGE",EDGE,{"disambiguationData":[OSD([subQ0,subQ1])]})});}
            var Q41;
            {var subQ0=sQuery(id+"F0.wireOp",EDGE,"E19");var subQ1=sQuery(id+"F0.wireOp",EDGE,"E30.trimOffspring");Q41=makeQuery(id+"F4.boolean.opBoolean","SPLIT",EDGE,{"disambiguationData":[TD([makeQuery(id+"F3.boolean.opBoolean","COPY",FACE,{"derivedFrom":makeQuery(id+"F3.opExtrude","SWEPT_FACE",FACE,{"disambiguationData":[OSD([sQuery(id+"F2.wireOp",EDGE,"E48")])]})})])],"derivedFrom":makeQuery(id+"F1.opExtrude","SWEPT_EDGE",EDGE,{"disambiguationData":[OSD([subQ0,subQ1])]})});}
            var Q42;
            {var subQ0=sQuery(id+"F0.wireOp",EDGE,"E20");var subQ1=sQuery(id+"F0.wireOp",EDGE,"E31.trimOffspring");Q42=makeQuery(id+"F4.boolean.opBoolean","SPLIT",EDGE,{"disambiguationData":[TD([makeQuery(id+"F3.boolean.opBoolean","COPY",FACE,{"derivedFrom":makeQuery(id+"F3.opExtrude","SWEPT_FACE",FACE,{"disambiguationData":[OSD([sQuery(id+"F2.wireOp",EDGE,"E48")])]})})])],"derivedFrom":makeQuery(id+"F1.opExtrude","SWEPT_EDGE",EDGE,{"disambiguationData":[OSD([subQ0,subQ1])]})});}
            var Q43;
            {var subQ0=sQuery(id+"F0.wireOp",EDGE,"E31.trimOffspring");var subQ1=sQuery(id+"F0.wireOp",EDGE,"E33");Q43=makeQuery(id+"F4.boolean.opBoolean","SPLIT",EDGE,{"disambiguationData":[TD([makeQuery(id+"F3.boolean.opBoolean","COPY",FACE,{"derivedFrom":makeQuery(id+"F3.opExtrude","SWEPT_FACE",FACE,{"disambiguationData":[OSD([sQuery(id+"F2.wireOp",EDGE,"E48")])]})})])],"derivedFrom":makeQuery(id+"F1.opExtrude","SWEPT_EDGE",EDGE,{"disambiguationData":[OSD([subQ0,subQ1])]})});}
            chamfer(context, id + "F10", {"entities" : qUnion([Q0, Q1, Q2, Q3, Q4, Q5, Q6, Q7, Q8, Q9, Q10, Q11, Q12, Q13, Q14, Q15, Q16, Q17, Q18, Q19, Q20, Q21, Q22, Q23, Q24, Q25, Q26, Q27, Q28, Q29, Q30, Q31, Q32, Q33, Q34, Q35, Q36, Q37, Q38, Q39, Q40, Q41, Q42, Q43]), "width" : 2 * mm, "tangentPropagation" : true});
        }
        {
            var Q0;
            {var subQ0=sQuery(id+"F2.wireOp",EDGE,"E46");Q0=makeQuery(id+"F8.boolean.opBoolean","INTERSECT",EDGE,{"derivedFrom":[makeQuery(id+"F6.boolean.opBoolean","SPLIT",FACE,{"disambiguationData":[TD([makeQuery(id+"F4.boolean.opBoolean","COPY",FACE,{"derivedFrom":makeQuery(id+"F4.opExtrude","SWEPT_FACE",FACE,{"disambiguationData":[OSD([subQ0])]})})])],"derivedFrom":makeQuery(id+"F4.boolean.opBoolean","COPY",FACE,{"derivedFrom":makeQuery(id+"F4.opExtrude","CAP_FACE",FACE,{"disambiguationData":[OSD([subQ0,sQuery(id+"F2.wireOp",EDGE,"E47"),sQuery(id+"F2.wireOp",EDGE,"E53"),sQuery(id+"F2.wireOp",EDGE,"E54")])],"isStart":false})})}),makeQuery(id+"F8.opExtrude","SWEPT_FACE",FACE,{"disambiguationData":[OSD([sQuery(id+"F7.wireOp",EDGE,"E59")])]})]});}
            var Q1;
            {var subQ0=sQuery(id+"F2.wireOp",EDGE,"E46");Q1=makeQuery(id+"F8.boolean.opBoolean","INTERSECT",EDGE,{"derivedFrom":[makeQuery(id+"F6.boolean.opBoolean","SPLIT",FACE,{"disambiguationData":[TD([makeQuery(id+"F4.boolean.opBoolean","COPY",FACE,{"derivedFrom":makeQuery(id+"F4.opExtrude","SWEPT_FACE",FACE,{"disambiguationData":[OSD([subQ0])]})})])],"derivedFrom":makeQuery(id+"F4.boolean.opBoolean","COPY",FACE,{"derivedFrom":makeQuery(id+"F4.opExtrude","CAP_FACE",FACE,{"disambiguationData":[OSD([subQ0,sQuery(id+"F2.wireOp",EDGE,"E47"),sQuery(id+"F2.wireOp",EDGE,"E53"),sQuery(id+"F2.wireOp",EDGE,"E54")])],"isStart":false})})}),makeQuery(id+"F8.opExtrude","SWEPT_FACE",FACE,{"disambiguationData":[OSD([sQuery(id+"F7.wireOp",EDGE,"E60")])]})]});}
            var Q2;
            {var subQ0=sQuery(id+"F2.wireOp",EDGE,"E47");Q2=makeQuery(id+"F9.boolean.opBoolean","INTERSECT",EDGE,{"derivedFrom":[makeQuery(id+"F6.boolean.opBoolean","SPLIT",FACE,{"disambiguationData":[TD([makeQuery(id+"F4.boolean.opBoolean","COPY",FACE,{"derivedFrom":makeQuery(id+"F4.opExtrude","SWEPT_FACE",FACE,{"disambiguationData":[OSD([subQ0])]})})])],"derivedFrom":makeQuery(id+"F4.boolean.opBoolean","COPY",FACE,{"derivedFrom":makeQuery(id+"F4.opExtrude","CAP_FACE",FACE,{"disambiguationData":[OSD([sQuery(id+"F2.wireOp",EDGE,"E46"),subQ0,sQuery(id+"F2.wireOp",EDGE,"E53"),sQuery(id+"F2.wireOp",EDGE,"E54")])],"isStart":false})})}),makeQuery(id+"F9.opExtrude","SWEPT_FACE",FACE,{"disambiguationData":[OSD([sQuery(id+"F7.wireOp",EDGE,"E62")])]})]});}
            var Q3;
            {var subQ0=sQuery(id+"F2.wireOp",EDGE,"E47");Q3=makeQuery(id+"F9.boolean.opBoolean","INTERSECT",EDGE,{"derivedFrom":[makeQuery(id+"F6.boolean.opBoolean","SPLIT",FACE,{"disambiguationData":[TD([makeQuery(id+"F4.boolean.opBoolean","COPY",FACE,{"derivedFrom":makeQuery(id+"F4.opExtrude","SWEPT_FACE",FACE,{"disambiguationData":[OSD([subQ0])]})})])],"derivedFrom":makeQuery(id+"F4.boolean.opBoolean","COPY",FACE,{"derivedFrom":makeQuery(id+"F4.opExtrude","CAP_FACE",FACE,{"disambiguationData":[OSD([sQuery(id+"F2.wireOp",EDGE,"E46"),subQ0,sQuery(id+"F2.wireOp",EDGE,"E53"),sQuery(id+"F2.wireOp",EDGE,"E54")])],"isStart":false})})}),makeQuery(id+"F9.opExtrude","SWEPT_FACE",FACE,{"disambiguationData":[OSD([sQuery(id+"F7.wireOp",EDGE,"E61")])]})]});}
            chamfer(context, id + "F11", {"entities" : qUnion([Q0, Q1, Q2, Q3]), "width" : 1 * mm, "tangentPropagation" : true});
        }
    });
